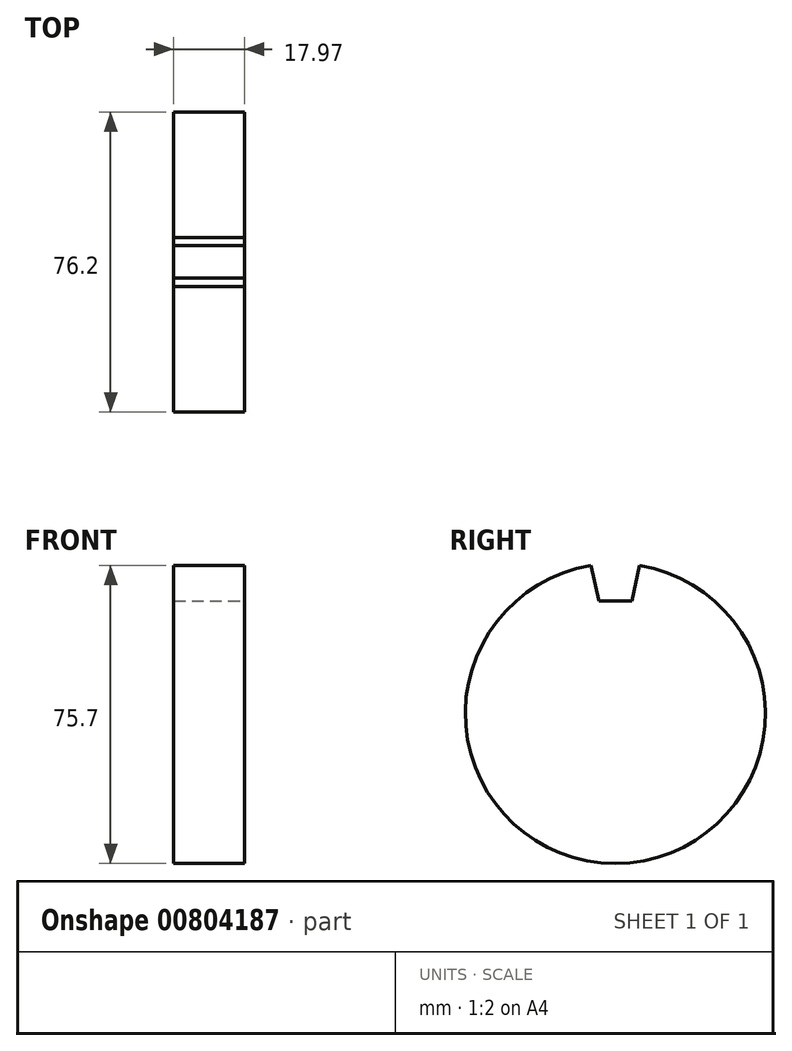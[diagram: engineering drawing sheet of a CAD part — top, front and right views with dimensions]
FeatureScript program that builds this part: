
annotation { "Feature Type Name" : "Feature", "Feature Type Description" : "" }
export const myFeature = defineFeature(function(context is Context, id is Id, definition is map)
    precondition{}
    {
        {
            var Q0;
            Q0=qCreatedBy(makeId("Front.planeOp"),FACE);
            var sketch = newSketch(context, id + "F0", { "sketchPlane" : qUnion([Q0])});
            skLineSegment(sketch, "E0.bottom", {"start": v(-17.97, 41.14) * mm, "end": v(0, 41.14) * mm});
            skLineSegment(sketch, "E0.top", {"start": v(-17.97, 3.04) * mm, "end": v(0, 3.04) * mm});
            skLineSegment(sketch, "E0.left", {"start": v(-17.97, 41.14) * mm, "end": v(-17.97, 3.04) * mm});
            skLineSegment(sketch, "E0.right", {"start": v(0, 41.14) * mm, "end": v(0, 3.04) * mm});
            skSolve(sketch);
        }
        {
            var Q0;
            Q0=makeQuery(id+"F0.imprint","IMPRINT",FACE,{"disambiguationData":[TD([[makeQuery(id+"F0.imprint","IMPRINT",EDGE,{"derivedFrom":sQuery(id+"F0.wireOp",EDGE,"E0.bottom")}),-1.0]])]});
            var Q1;
            Q1=sQuery(id+"F0.wireOp",EDGE,"E0.top");
            revolve(context, id + "F1", {"surfaceOperationType" : NewSurfaceOperationType.NEW, "entities" : qUnion([Q0]), "axis" : qUnion([Q1]), "revolveType" : RevolveType.FULL});
        }
        {
            var Q0;
            Q0=makeQuery(id+"F1.opRevolve","SWEPT_FACE",FACE,{"disambiguationData":[OSD([sQuery(id+"F0.wireOp",EDGE,"E0.right")])]});
            var sketch = newSketch(context, id + "F2", { "sketchPlane" : qUnion([Q0])});
            skLineSegment(sketch, "E1", {"start": v(-4.12, 31.67) * mm, "end": v(0, 31.67) * mm});
            skLineSegment(sketch, "E2", {"start": v(4.2, 31.67) * mm, "end": v(0, 31.67) * mm});
            skLineSegment(sketch, "E3", {"start": v(0, 41.14) * mm, "end": v(0, 31.67) * mm});
            skLineSegment(sketch, "E4", {"start": v(0, 41.14) * mm, "end": v(-6.33, 41.14) * mm});
            skLineSegment(sketch, "E5", {"start": v(0, 41.14) * mm, "end": v(6.3, 41.14) * mm});
            skLineSegment(sketch, "E6", {"start": v(6.3, 41.14) * mm, "end": v(4.2, 31.67) * mm});
            skLineSegment(sketch, "E7", {"start": v(-6.33, 41.14) * mm, "end": v(-4.12, 31.67) * mm});
            skSolve(sketch);
        }
        {
            var Q0;
            {var subQ0=sQuery(id+"F2.wireOp",EDGE,"E1");Q0=makeQuery(id+"F2.imprint","IMPRINT",FACE,{"disambiguationData":[TD([[makeQuery(id+"F2.imprint","IMPRINT",EDGE,{"derivedFrom":subQ0}),1.0]])]});}
            var Q1;
            {var subQ0=sQuery(id+"F2.wireOp",EDGE,"E2");Q1=makeQuery(id+"F2.imprint","IMPRINT",FACE,{"disambiguationData":[TD([[makeQuery(id+"F2.imprint","IMPRINT",EDGE,{"derivedFrom":subQ0}),-1.0]])]});}
            extrude(context, id + "F3", {"entities" : qUnion([Q0, Q1]), "operationType" : NewBodyOperationType.REMOVE, "oppositeDirection" : true, "depth" : 25.4 * mm, "offsetDistance" : 25.4 * mm});
        }
    });
